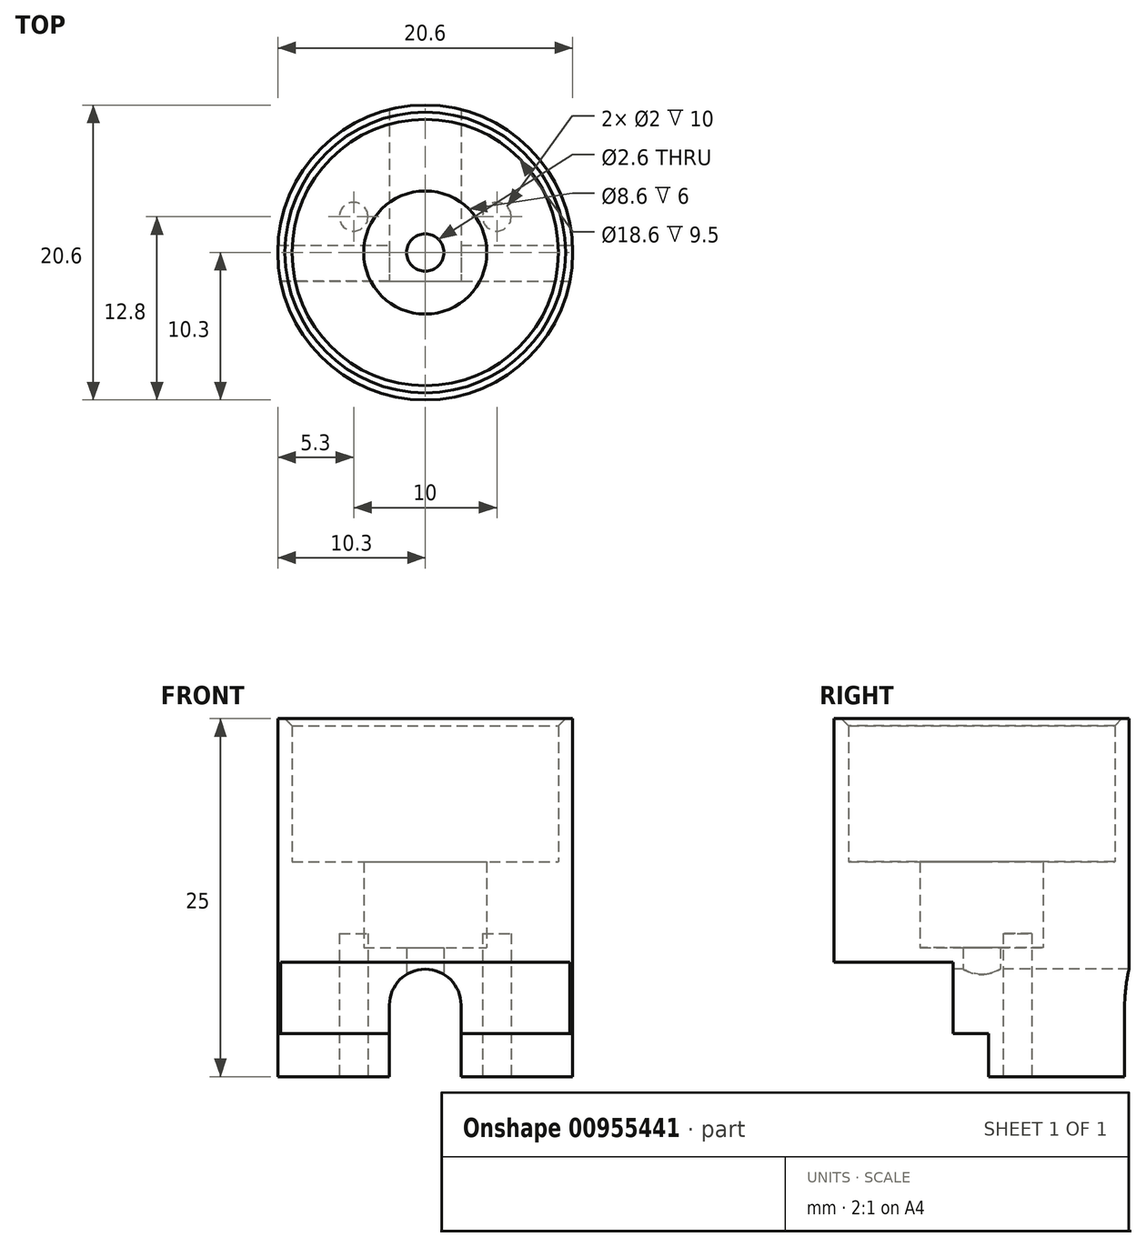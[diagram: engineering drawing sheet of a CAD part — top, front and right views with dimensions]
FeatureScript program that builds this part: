
annotation { "Feature Type Name" : "Feature", "Feature Type Description" : "" }
export const myFeature = defineFeature(function(context is Context, id is Id, definition is map)
    precondition{}
    {
        {
            var Q0;
            Q0=qCreatedBy(makeId("Front.planeOp"),FACE);
            var sketch = newSketch(context, id + "F0", { "sketchPlane" : qUnion([Q0])});
            skLineSegment(sketch, "E0", {"start": v(-1.3, 0) * mm, "end": v(-1.3, 9) * mm});
            skLineSegment(sketch, "E1", {"start": v(-1.3, 9) * mm, "end": v(-4.3, 9) * mm});
            skLineSegment(sketch, "E2", {"start": v(-4.3, 9) * mm, "end": v(-4.3, 15) * mm});
            skLineSegment(sketch, "E3", {"start": v(-4.3, 15) * mm, "end": v(-9.3, 15) * mm});
            skLineSegment(sketch, "E4", {"start": v(-9.3, 15) * mm, "end": v(-9.3, 25) * mm});
            skLineSegment(sketch, "E5", {"start": v(-9.3, 25) * mm, "end": v(-10.3, 25) * mm});
            skLineSegment(sketch, "E6", {"start": v(-10.3, 25) * mm, "end": v(-10.3, 0) * mm});
            skLineSegment(sketch, "E7", {"start": v(-10.3, 0) * mm, "end": v(-1.3, 0) * mm});
            skLineSegment(sketch, "E8", {"start": v(0, -5.77) * mm, "end": v(0, 22.45) * mm, "construction": true});
            skSolve(sketch);
        }
        {
            var Q0;
            Q0=makeQuery(id+"F0.imprint","IMPRINT",FACE,{"disambiguationData":[TD([[makeQuery(id+"F0.imprint","IMPRINT",EDGE,{"derivedFrom":sQuery(id+"F0.wireOp",EDGE,"E0")}),1.0]])]});
            var Q1;
            Q1=sQuery(id+"F0.wireOp",EDGE,"E8");
            revolve(context, id + "F1", {"surfaceOperationType" : NewSurfaceOperationType.NEW, "entities" : qUnion([Q0]), "axis" : qUnion([Q1]), "revolveType" : RevolveType.FULL});
        }
        {
            var Q0;
            Q0=qCreatedBy(makeId("Front.planeOp"),FACE);
            var sketch = newSketch(context, id + "F2", { "sketchPlane" : qUnion([Q0])});
            skLineSegment(sketch, "E9", {"start": v(-2.5, 0) * mm, "end": v(-2.5, 5) * mm});
            skCircle(sketch, "E10", {"center": v(0, 5) * mm, "radius": 2.5 * mm});
            skLineSegment(sketch, "E11", {"start": v(-2.5, 0) * mm, "end": v(0, 0) * mm});
            skLineSegment(sketch, "E12", {"start": v(2.5, 5) * mm, "end": v(2.5, 0) * mm});
            skLineSegment(sketch, "E13", {"start": v(2.5, 0) * mm, "end": v(0, 0) * mm});
            skSolve(sketch);
        }
        {
            var Q0;
            Q0 = qSketchRegion(id + "F2", true);
            extrude(context, id + "F3", {"entities" : qUnion([Q0]), "operationType" : NewBodyOperationType.REMOVE, "endBound" : BoundingType.SYMMETRIC, "oppositeDirection" : true, "depth" : 36 * mm, "offsetDistance" : 25 * mm});
        }
        {
            var Q0;
            Q0=qCreatedBy(makeId("Right.planeOp"),FACE);
            var sketch = newSketch(context, id + "F4", { "sketchPlane" : qUnion([Q0])});
            skLineSegment(sketch, "E14.bottom", {"start": v(0, 0) * mm, "end": v(-10.3, 0) * mm});
            skLineSegment(sketch, "E14.top", {"start": v(0, 8) * mm, "end": v(-10.3, 8) * mm});
            skLineSegment(sketch, "E14.left", {"start": v(0, 0) * mm, "end": v(0, 8) * mm});
            skLineSegment(sketch, "E14.right", {"start": v(-10.3, 0) * mm, "end": v(-10.3, 8) * mm});
            skLineSegment(sketch, "E15", {"start": v(-2, 0) * mm, "end": v(-2, 8) * mm});
            skSolve(sketch);
        }
        {
            var Q0;
            {var subQ0=sQuery(id+"F4.wireOp",EDGE,"E14.right");Q0=makeQuery(id+"F4.imprint","IMPRINT",FACE,{"disambiguationData":[TD([[makeQuery(id+"F4.imprint","IMPRINT",EDGE,{"derivedFrom":subQ0}),-1.0]])]});}
            extrude(context, id + "F5", {"entities" : qUnion([Q0]), "operationType" : NewBodyOperationType.REMOVE, "endBound" : BoundingType.SYMMETRIC, "oppositeDirection" : true, "depth" : 20.6 * mm, "offsetDistance" : 25 * mm});
        }
        {
            var Q0;
            Q0=makeQuery(id+"F5.boolean.opBoolean","COPY",FACE,{"derivedFrom":makeQuery(id+"F5.opExtrude","SWEPT_FACE",FACE,{"disambiguationData":[OSD([sQuery(id+"F4.wireOp",EDGE,"E15")])]})});
            var sketch = newSketch(context, id + "F6", { "sketchPlane" : qUnion([Q0])});
            skLineSegment(sketch, "E16.bottom", {"start": v(0, 0) * mm, "end": v(10.3, 0) * mm});
            skLineSegment(sketch, "E16.top", {"start": v(0, 3) * mm, "end": v(10.3, 3) * mm});
            skLineSegment(sketch, "E16.left", {"start": v(0, 0) * mm, "end": v(0, 3) * mm});
            skLineSegment(sketch, "E16.right", {"start": v(10.3, 0) * mm, "end": v(10.3, 3) * mm});
            skLineSegment(sketch, "E17.bottom", {"start": v(0, 0) * mm, "end": v(-10.3, 0) * mm});
            skLineSegment(sketch, "E17.top", {"start": v(0, 3) * mm, "end": v(-10.3, 3) * mm});
            skLineSegment(sketch, "E17.right", {"start": v(-10.3, 0) * mm, "end": v(-10.3, 3) * mm});
            skSolve(sketch);
        }
        {
            var Q0;
            {var subQ0=sQuery(id+"F6.wireOp",EDGE,"E17.bottom");var subQ1=makeQuery(id+"F5.opExtrude","SWEPT_FACE",FACE,{"disambiguationData":[OSD([sQuery(id+"F4.wireOp",EDGE,"E15")])]});var subQ2=makeQuery(id+"F5.boolean.opBoolean","INTERSECT",EDGE,{"derivedFrom":[makeQuery(id+"F3.boolean.opBoolean","COPY",FACE,{"derivedFrom":makeQuery(id+"F3.opExtrude","SWEPT_FACE",FACE,{"disambiguationData":[OSD([sQuery(id+"F2.wireOp",EDGE,"E9")])]})}),subQ1]});var subQ3=makeQuery(id+"F6.imprint","INTERSECT",VERTEX,{"derivedFrom":[subQ2,subQ0]});var subQ4=makeQuery(id+"F5.boolean.opBoolean","INTERSECT",EDGE,{"disambiguationData":[OD(0.0)],"derivedFrom":[makeQuery(id+"F1.opRevolve","SWEPT_FACE",FACE,{"disambiguationData":[OSD([sQuery(id+"F0.wireOp",EDGE,"E6")])]}),subQ1]});var subQ5=makeQuery(id+"F6.imprint","INTERSECT",VERTEX,{"derivedFrom":[subQ4,subQ0]});Q0=makeQuery(id+"F6.imprint","IMPRINT",FACE,{"disambiguationData":[TD([[makeQuery(id+"F6.imprint","IMPRINT",EDGE,{"disambiguationData":[TD([[subQ3,1.0],[subQ5,-1.0]])],"derivedFrom":subQ0}),1.0]])]});}
            var Q1;
            {var subQ0=sQuery(id+"F6.wireOp",EDGE,"E16.bottom");var subQ1=makeQuery(id+"F5.opExtrude","SWEPT_FACE",FACE,{"disambiguationData":[OSD([sQuery(id+"F4.wireOp",EDGE,"E15")])]});var subQ2=makeQuery(id+"F5.boolean.opBoolean","INTERSECT",EDGE,{"derivedFrom":[makeQuery(id+"F3.boolean.opBoolean","COPY",FACE,{"derivedFrom":makeQuery(id+"F3.opExtrude","SWEPT_FACE",FACE,{"disambiguationData":[OSD([sQuery(id+"F2.wireOp",EDGE,"E12")])]})}),subQ1]});var subQ3=makeQuery(id+"F6.imprint","INTERSECT",VERTEX,{"derivedFrom":[subQ2,subQ0]});Q1=makeQuery(id+"F6.imprint","IMPRINT",FACE,{"disambiguationData":[TD([[makeQuery(id+"F6.imprint","IMPRINT",EDGE,{"disambiguationData":[TD([[subQ3,-1.0]])],"derivedFrom":subQ0}),1.0]])]});}
            var Q2;
            {var subQ3=sQuery(id+"F6.wireOp",EDGE,"E16.right");Q2=makeQuery(id+"F6.imprint","IMPRINT",FACE,{"disambiguationData":[TD([[makeQuery(id+"F6.imprint","IMPRINT",EDGE,{"derivedFrom":subQ3}),1.0]])]});}
            var Q3;
            {var subQ3=sQuery(id+"F6.wireOp",EDGE,"E17.right");Q3=makeQuery(id+"F6.imprint","IMPRINT",FACE,{"disambiguationData":[TD([[makeQuery(id+"F6.imprint","IMPRINT",EDGE,{"derivedFrom":subQ3}),-1.0]])]});}
            extrude(context, id + "F7", {"entities" : qUnion([Q0, Q1, Q2, Q3]), "operationType" : NewBodyOperationType.REMOVE, "oppositeDirection" : true, "depth" : 2.5 * mm, "offsetDistance" : 25 * mm});
        }
        {
            var Q0;
            Q0=makeQuery(id+"F1.opRevolve","SWEPT_EDGE",EDGE,{"disambiguationData":[OSD([sQuery(id+"F0.wireOp",EDGE,"E4"),sQuery(id+"F0.wireOp",EDGE,"E5")])]});
            chamfer(context, id + "F8", {"entities" : qUnion([Q0]), "width" : 0.5 * mm, "tangentPropagation" : true});
        }
        {
            var Q0;
            Q0=makeQuery(id+"F3.boolean.opBoolean","SPLIT",FACE,{"disambiguationData":[TD([makeQuery(id+"F3.opExtrude","SWEPT_FACE",FACE,{"disambiguationData":[OSD([sQuery(id+"F2.wireOp",EDGE,"E12")])]})])],"derivedFrom":makeQuery(id+"F1.opRevolve","SWEPT_FACE",FACE,{"disambiguationData":[OSD([sQuery(id+"F0.wireOp",EDGE,"E7")])]})});
            var sketch = newSketch(context, id + "F9", { "sketchPlane" : qUnion([Q0])});
            skCircle(sketch, "E18", {"center": v(-5, -2.5) * mm, "radius": 1 * mm});
            skCircle(sketch, "E19", {"center": v(5, -2.5) * mm, "radius": 1 * mm});
            skSolve(sketch);
        }
        {
            var Q0;
            Q0=makeQuery(id+"F9.imprint","IMPRINT",FACE,{"disambiguationData":[TD([[makeQuery(id+"F9.imprint","IMPRINT",EDGE,{"derivedFrom":sQuery(id+"F9.wireOp",EDGE,"E18")}),1.0]])]});
            var Q1;
            Q1=makeQuery(id+"F9.imprint","IMPRINT",FACE,{"disambiguationData":[TD([[makeQuery(id+"F9.imprint","IMPRINT",EDGE,{"derivedFrom":sQuery(id+"F9.wireOp",EDGE,"E19")}),1.0]])]});
            extrude(context, id + "F10", {"entities" : qUnion([Q0, Q1]), "operationType" : NewBodyOperationType.REMOVE, "oppositeDirection" : true, "depth" : 10 * mm, "offsetDistance" : 25 * mm});
        }
    });
